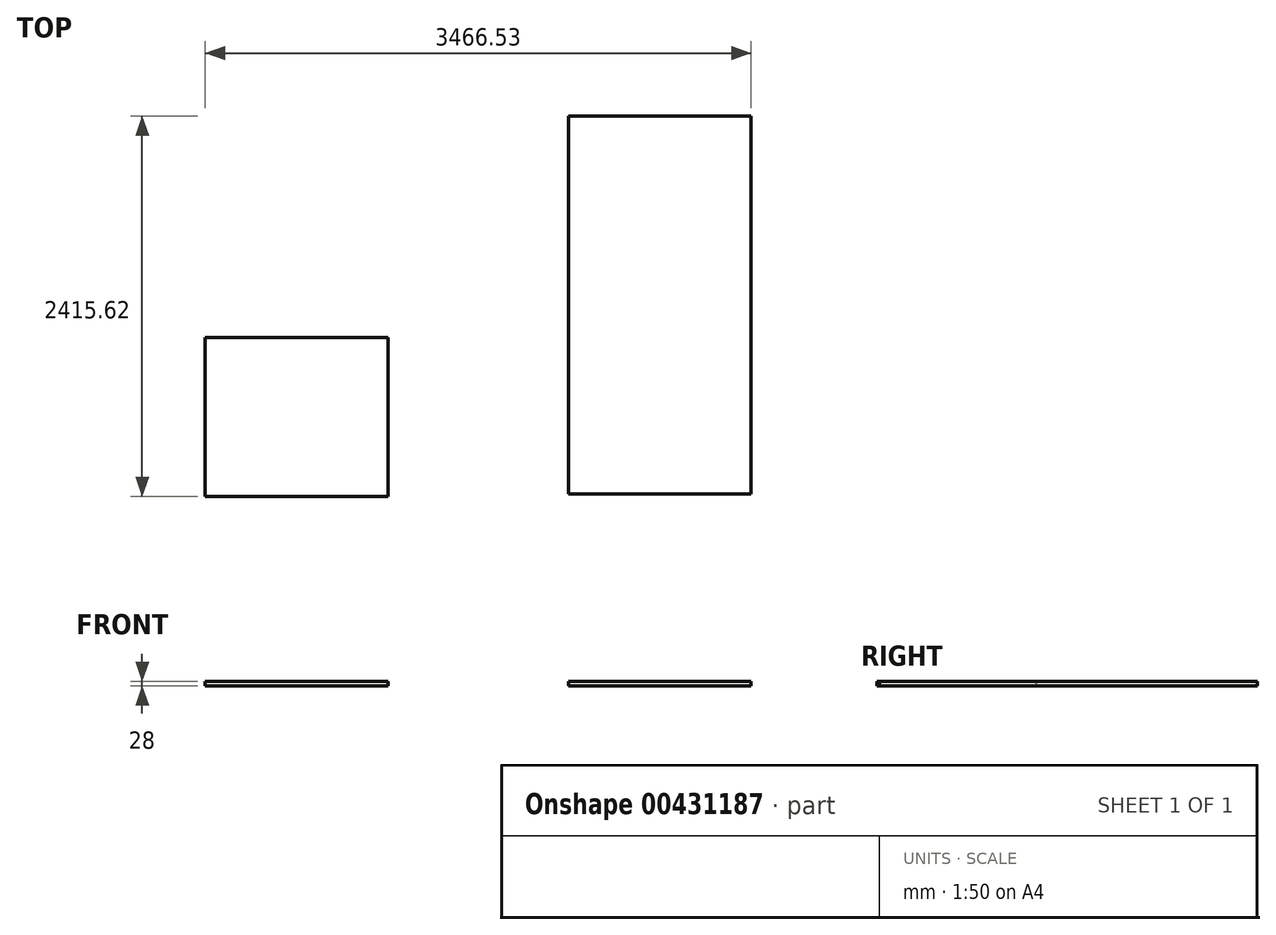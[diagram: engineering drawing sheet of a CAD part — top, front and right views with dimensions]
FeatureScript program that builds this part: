
annotation { "Feature Type Name" : "Feature", "Feature Type Description" : "" }
export const myFeature = defineFeature(function(context is Context, id is Id, definition is map)
    precondition{}
    {
        {
            var Q0;
            Q0=qCreatedBy(makeId("Top.planeOp"),FACE);
            var sketch = newSketch(context, id + "F0", { "sketchPlane" : qUnion([Q0])});
            skLineSegment(sketch, "E0", {"start": v(0, 0) * mm, "end": v(1160, 0) * mm});
            skLineSegment(sketch, "E1", {"start": v(1160, 0) * mm, "end": v(1160, -1010) * mm});
            skLineSegment(sketch, "E2", {"start": v(1160, -1010) * mm, "end": v(0, -1010) * mm});
            skLineSegment(sketch, "E3", {"start": v(0, -1010) * mm, "end": v(0, 0) * mm});
            skSolve(sketch);
        }
        {
            var Q0;
            Q0=qCreatedBy(makeId("Top.planeOp"),FACE);
            var sketch = newSketch(context, id + "F1", { "sketchPlane" : qUnion([Q0])});
            skLineSegment(sketch, "E4", {"start": v(2306.53, 1405.62) * mm, "end": v(3466.53, 1405.62) * mm});
            skLineSegment(sketch, "E5", {"start": v(3466.53, 1405.62) * mm, "end": v(3466.53, -994.38) * mm});
            skLineSegment(sketch, "E6", {"start": v(3466.53, -994.38) * mm, "end": v(2306.53, -994.38) * mm});
            skLineSegment(sketch, "E7", {"start": v(2306.53, -994.38) * mm, "end": v(2306.53, 1405.62) * mm});
            skSolve(sketch);
        }
        {
            var Q0;
            Q0=makeQuery(id+"F0.imprint","IMPRINT",FACE,{"disambiguationData":[TD([[makeQuery(id+"F0.imprint","IMPRINT",EDGE,{"derivedFrom":sQuery(id+"F0.wireOp",EDGE,"E0")}),-1.0]])]});
            var Q1;
            Q1=makeQuery(id+"F1.imprint","IMPRINT",FACE,{"disambiguationData":[TD([[makeQuery(id+"F1.imprint","IMPRINT",EDGE,{"derivedFrom":sQuery(id+"F1.wireOp",EDGE,"E4")}),-1.0]])]});
            extrude(context, id + "F2", {"entities" : qUnion([Q0, Q1]), "depth" : 28 * mm});
        }
    });
